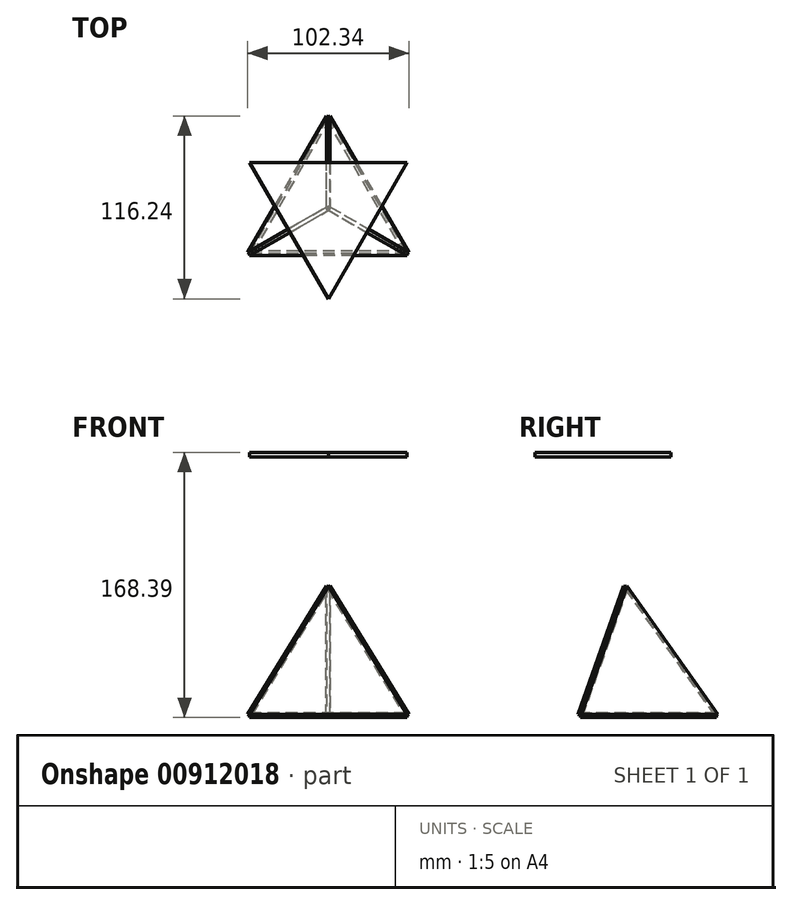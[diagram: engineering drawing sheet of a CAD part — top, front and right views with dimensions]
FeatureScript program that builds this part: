
annotation { "Feature Type Name" : "Feature", "Feature Type Description" : "" }
export const myFeature = defineFeature(function(context is Context, id is Id, definition is map)
    precondition{}
    {
        {
            var Q0;
            Q0=qCreatedBy(makeId("Top.planeOp"),FACE);
            var sketch = newSketch(context, id + "F0", { "sketchPlane" : qUnion([Q0])});
            skCircle(sketch, "E0.cCircle", {"center": v(0, 0) * mm, "radius": 28.87 * mm, "construction": true});
            skLineSegment(sketch, "E0.0", {"start": v(0, 57.74) * mm, "end": v(50, -28.87) * mm});
            skLineSegment(sketch, "E0.1", {"start": v(50, -28.87) * mm, "end": v(-50, -28.87) * mm});
            skLineSegment(sketch, "E0.2", {"start": v(-50, -28.87) * mm, "end": v(0, 57.74) * mm});
            skPoint(sketch, "E0.0.midPoint", {"position": v(25, 14.43) * mm});
            skSolve(sketch);
        }
        {
            var Q0;
            Q0=makeQuery(id+"F0.imprint","IMPRINT",FACE,{"disambiguationData":[TD([[makeQuery(id+"F0.imprint","IMPRINT",EDGE,{"derivedFrom":sQuery(id+"F0.wireOp",EDGE,"E0.0")}),-1.0]])]});
            extrude(context, id + "F1", {"entities" : qUnion([Q0]), "depth" : 3 * mm, "offsetDistance" : 25 * mm});
        }
        {
            var Q0;
            Q0=makeQuery(id+"F1.opExtrude","SWEPT_FACE",FACE,{"disambiguationData":[OSD([sQuery(id+"F0.wireOp",EDGE,"E0.1")])]});
            var sketch = newSketch(context, id + "F2", { "sketchPlane" : qUnion([Q0])});
            skLineSegment(sketch, "E1", {"start": v(-50, 1.5) * mm, "end": v(50, 1.5) * mm});
            skSolve(sketch);
        }
        {
            var Q0;
            Q0=makeQuery(id+"F1.opExtrude","SWEPT_BODY",BODY,{"disambiguationData":[OSD([sQuery(id+"F0.wireOp",EDGE,"E0.0"),sQuery(id+"F0.wireOp",EDGE,"E0.1"),sQuery(id+"F0.wireOp",EDGE,"E0.2")])]});
            transform(context, id + "F3", {"entities" : qUnion([Q0]), "transformType" : TransformType.TRANSLATION_3D, "dx" : 0 * mm, "dy" : 0 * mm, "dz" : 0 * mm, "makeCopy" : true});
        }
        {
            var Q0;
            Q0=makeQuery(id+"F3.opPattern","COPY",BODY,{"derivedFrom":makeQuery(id+"F1.opExtrude","SWEPT_BODY",BODY,{"disambiguationData":[OSD([sQuery(id+"F0.wireOp",EDGE,"E0.0"),sQuery(id+"F0.wireOp",EDGE,"E0.1"),sQuery(id+"F0.wireOp",EDGE,"E0.2")])]}),"instanceName":"1"});
            var Q1;
            Q1=sQuery(id+"F2.wireOp",EDGE,"E1");
            transform(context, id + "F4", {"entities" : qUnion([Q0]), "transformType" : TransformType.ROTATION, "transformAxis" : qUnion([Q1]), "angle" : 70.53 * degree, "makeCopy" : false});
        }
        {
            var Q0;
            Q0=makeQuery(id+"F3.opPattern","COPY",FACE,{"derivedFrom":makeQuery(id+"F1.opExtrude","SWEPT_FACE",FACE,{"disambiguationData":[OSD([sQuery(id+"F0.wireOp",EDGE,"E0.0")])]}),"instanceName":"1"});
            var sketch = newSketch(context, id + "F5", { "sketchPlane" : qUnion([Q0])});
            skLineSegment(sketch, "E2", {"start": v(-6.63, 72.6) * mm, "end": v(-35.77, -22.59) * mm});
            skPoint(sketch, "E2.startSnap0", {"position": v(-6.63, 73.03) * mm});
            skPoint(sketch, "E2.endSnap0", {"position": v(-35.9, -22.59) * mm});
            skSolve(sketch);
        }
        {
            var Q0;
            Q0=makeQuery(id+"F3.opPattern","COPY",BODY,{"derivedFrom":makeQuery(id+"F1.opExtrude","SWEPT_BODY",BODY,{"disambiguationData":[OSD([sQuery(id+"F0.wireOp",EDGE,"E0.0"),sQuery(id+"F0.wireOp",EDGE,"E0.1"),sQuery(id+"F0.wireOp",EDGE,"E0.2")])]}),"instanceName":"1"});
            transform(context, id + "F6", {"entities" : qUnion([Q0]), "transformType" : TransformType.TRANSLATION_3D, "dx" : 0 * mm, "dy" : 0 * mm, "dz" : 0 * mm, "makeCopy" : true});
        }
        {
            var Q0;
            Q0=makeQuery(id+"F6.opPattern","COPY",BODY,{"derivedFrom":makeQuery(id+"F3.opPattern","COPY",BODY,{"derivedFrom":makeQuery(id+"F1.opExtrude","SWEPT_BODY",BODY,{"disambiguationData":[OSD([sQuery(id+"F0.wireOp",EDGE,"E0.0"),sQuery(id+"F0.wireOp",EDGE,"E0.1"),sQuery(id+"F0.wireOp",EDGE,"E0.2")])]}),"instanceName":"1"}),"instanceName":"1"});
            var Q1;
            Q1=sQuery(id+"F5.wireOp",EDGE,"E2");
            var Q2;
            Q2=sQuery(id+"F5.wireOp",EDGE,"E2");
            transform(context, id + "F7", {"entities" : qUnion([Q0]), "transformType" : TransformType.ROTATION, "transformAxis" : qUnion([Q2]), "angle" : 70.53 * degree, "makeCopy" : false});
        }
        {
            var Q0;
            Q0=makeQuery(id+"F3.opPattern","COPY",FACE,{"derivedFrom":makeQuery(id+"F1.opExtrude","SWEPT_FACE",FACE,{"disambiguationData":[OSD([sQuery(id+"F0.wireOp",EDGE,"E0.2")])]}),"instanceName":"1"});
            var sketch = newSketch(context, id + "F8", { "sketchPlane" : qUnion([Q0])});
            skLineSegment(sketch, "E3", {"start": v(35.9, -22.59) * mm, "end": v(6.63, 73.03) * mm});
            skSolve(sketch);
        }
        {
            var Q0;
            Q0=makeQuery(id+"F6.opPattern","COPY",BODY,{"derivedFrom":makeQuery(id+"F3.opPattern","COPY",BODY,{"derivedFrom":makeQuery(id+"F1.opExtrude","SWEPT_BODY",BODY,{"disambiguationData":[OSD([sQuery(id+"F0.wireOp",EDGE,"E0.0"),sQuery(id+"F0.wireOp",EDGE,"E0.1"),sQuery(id+"F0.wireOp",EDGE,"E0.2")])]}),"instanceName":"1"}),"instanceName":"1"});
            transform(context, id + "F9", {"entities" : qUnion([Q0]), "transformType" : TransformType.TRANSLATION_3D, "dx" : 0 * mm, "dy" : 0 * mm, "dz" : 0 * mm, "makeCopy" : true});
        }
        {
            var Q0;
            Q0=makeQuery(id+"F3.opPattern","COPY",BODY,{"derivedFrom":makeQuery(id+"F1.opExtrude","SWEPT_BODY",BODY,{"disambiguationData":[OSD([sQuery(id+"F0.wireOp",EDGE,"E0.0"),sQuery(id+"F0.wireOp",EDGE,"E0.1"),sQuery(id+"F0.wireOp",EDGE,"E0.2")])]}),"instanceName":"1"});
            transform(context, id + "F10", {"entities" : qUnion([Q0]), "transformType" : TransformType.TRANSLATION_3D, "dx" : 0 * mm, "dy" : 0 * mm, "dz" : 0 * mm, "makeCopy" : true});
        }
        {
            var Q0;
            Q0=makeQuery(id+"F10.opPattern","COPY",BODY,{"derivedFrom":makeQuery(id+"F3.opPattern","COPY",BODY,{"derivedFrom":makeQuery(id+"F1.opExtrude","SWEPT_BODY",BODY,{"disambiguationData":[OSD([sQuery(id+"F0.wireOp",EDGE,"E0.0"),sQuery(id+"F0.wireOp",EDGE,"E0.1"),sQuery(id+"F0.wireOp",EDGE,"E0.2")])]}),"instanceName":"1"}),"instanceName":"1"});
            var Q1;
            Q1=sQuery(id+"F8.wireOp",EDGE,"E3");
            var Q2;
            Q2=sQuery(id+"F8.wireOp",EDGE,"E3");
            transform(context, id + "F11", {"entities" : qUnion([Q0]), "transformType" : TransformType.ROTATION, "transformAxis" : qUnion([Q2]), "angle" : 70.53 * degree, "makeCopy" : false});
        }
        {
            var Q0;
            Q0=makeQuery(id+"F1.opExtrude","SWEPT_BODY",BODY,{"disambiguationData":[OSD([sQuery(id+"F0.wireOp",EDGE,"E0.0"),sQuery(id+"F0.wireOp",EDGE,"E0.1"),sQuery(id+"F0.wireOp",EDGE,"E0.2")])]});
            transform(context, id + "F12", {"entities" : qUnion([Q0]), "transformType" : TransformType.TRANSLATION_3D, "dx" : 0 * mm, "dy" : 0 * mm, "dz" : 0 * mm, "makeCopy" : true});
        }
        {
            var Q0;
            Q0=qCreatedBy(makeId("Front.planeOp"),FACE);
            var sketch = newSketch(context, id + "F13", { "sketchPlane" : qUnion([Q0])});
            skLineSegment(sketch, "E4", {"start": v(0, 84.2) * mm, "end": v(59.79, 84.2) * mm});
            skSolve(sketch);
        }
        {
            var Q0;
            Q0=makeQuery(id+"F12.opPattern","COPY",BODY,{"derivedFrom":makeQuery(id+"F1.opExtrude","SWEPT_BODY",BODY,{"disambiguationData":[OSD([sQuery(id+"F0.wireOp",EDGE,"E0.0"),sQuery(id+"F0.wireOp",EDGE,"E0.1"),sQuery(id+"F0.wireOp",EDGE,"E0.2")])]}),"instanceName":"1"});
            var Q1;
            Q1=sQuery(id+"F13.wireOp",EDGE,"E4");
            transform(context, id + "F14", {"entities" : qUnion([Q0]), "transformType" : TransformType.ROTATION, "transformAxis" : qUnion([Q1]), "angle" : 180 * degree, "makeCopy" : false});
        }
    });
